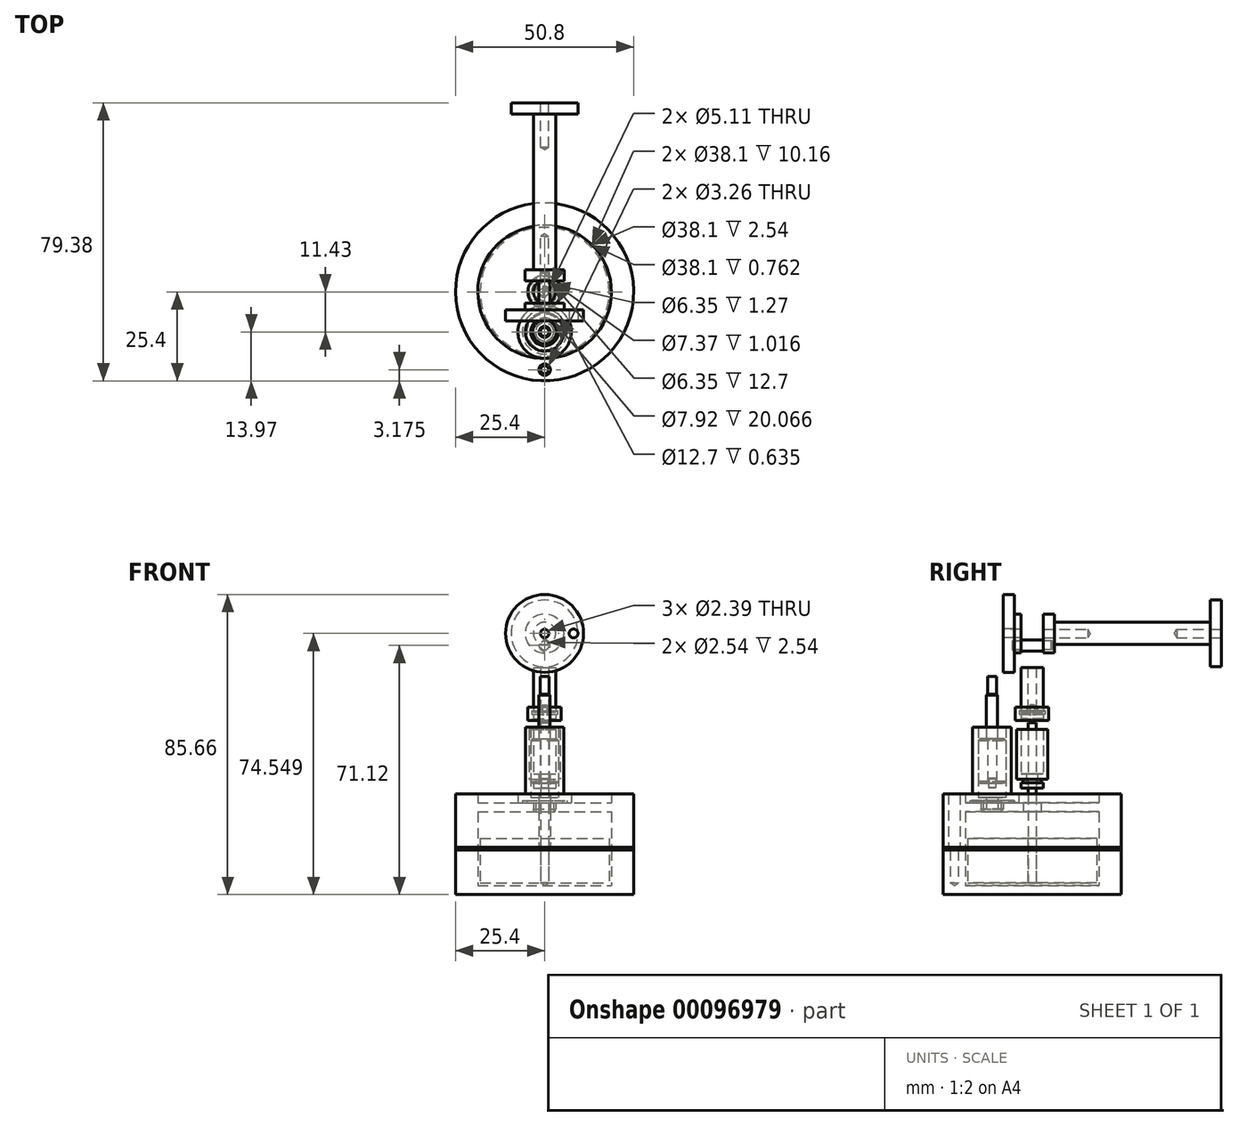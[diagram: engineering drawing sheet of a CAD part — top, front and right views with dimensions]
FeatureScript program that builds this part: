
annotation { "Feature Type Name" : "Feature", "Feature Type Description" : "" }
export const myFeature = defineFeature(function(context is Context, id is Id, definition is map)
    precondition{}
    {
        {
            assignVariable(context, id + "F0", {"name" : "RevolveDeg", "anyValue" : 360});
        }
        {
            var Q0;
            Q0=qCreatedBy(makeId("Right.planeOp"),FACE);
            var sketch = newSketch(context, id + "F1", { "sketchPlane" : qUnion([Q0])});
            skLineSegment(sketch, "E0", {"start": v(0, 0) * mm, "end": v(0, 183.81) * mm, "construction": true});
            skLineSegment(sketch, "E1", {"start": v(0, 0) * mm, "end": v(25.4, 0) * mm});
            skLineSegment(sketch, "E2", {"start": v(25.4, 12.7) * mm, "end": v(19.05, 12.7) * mm});
            skLineSegment(sketch, "E3", {"start": v(19.05, 12.7) * mm, "end": v(19.05, 2.54) * mm});
            skLineSegment(sketch, "E4", {"start": v(19.05, 2.54) * mm, "end": v(0, 2.54) * mm});
            skLineSegment(sketch, "E5", {"start": v(0, 2.54) * mm, "end": v(0, 0) * mm});
            skLineSegment(sketch, "E6", {"start": v(25.4, 12.7) * mm, "end": v(25.4, 0) * mm});
            skSolve(sketch);
        }
        {
            var Q0;
            Q0=qSketchRegion(id+"F1",true);
            var Q1;
            Q1=sQuery(id+"F1.wireOp",EDGE,"E0");
            revolve(context, id + "F2", {"entities" : qUnion([Q0]), "axis" : qUnion([Q1]), "revolveType" : RevolveType.ONE_DIRECTION, "angle" : (getVariable(context, 'RevolveDeg')) * degree});
        }
        {
            var Q0;
            Q0=qCreatedBy(makeId("Right.planeOp"),FACE);
            var sketch = newSketch(context, id + "F3", { "sketchPlane" : qUnion([Q0])});
            skLineSegment(sketch, "E7", {"start": v(0, 0) * mm, "end": v(0, 44.02) * mm, "construction": true});
            skLineSegment(sketch, "E8.bottom", {"start": v(19.05, 13.46) * mm, "end": v(25.4, 13.46) * mm});
            skLineSegment(sketch, "E8.top", {"start": v(19.05, 12.7) * mm, "end": v(25.4, 12.7) * mm});
            skLineSegment(sketch, "E8.left", {"start": v(19.05, 13.46) * mm, "end": v(19.05, 12.7) * mm});
            skLineSegment(sketch, "E8.right", {"start": v(25.4, 13.46) * mm, "end": v(25.4, 12.7) * mm});
            skSolve(sketch);
        }
        {
            var Q0;
            Q0=qSketchRegion(id+"F3",true);
            var Q1;
            Q1=sQuery(id+"F1.wireOp",EDGE,"E0");
            revolve(context, id + "F4", {"entities" : qUnion([Q0]), "axis" : qUnion([Q1]), "revolveType" : RevolveType.ONE_DIRECTION, "angle" : (getVariable(context, 'RevolveDeg')) * degree});
        }
        {
            var Q0;
            Q0=qCreatedBy(makeId("Right.planeOp"),FACE);
            var sketch = newSketch(context, id + "F5", { "sketchPlane" : qUnion([Q0])});
            skLineSegment(sketch, "E9", {"start": v(0, 0) * mm, "end": v(0, 65.3) * mm, "construction": true});
            skLineSegment(sketch, "E10", {"start": v(2.55, 23.62) * mm, "end": v(19.05, 23.62) * mm});
            skLineSegment(sketch, "E11", {"start": v(19.05, 23.62) * mm, "end": v(19.05, 13.46) * mm});
            skLineSegment(sketch, "E12", {"start": v(19.05, 13.46) * mm, "end": v(25.4, 13.46) * mm});
            skLineSegment(sketch, "E13", {"start": v(19.05, 26.16) * mm, "end": v(2.55, 26.16) * mm});
            skLineSegment(sketch, "E14", {"start": v(19.05, 28.7) * mm, "end": v(25.4, 28.7) * mm});
            skLineSegment(sketch, "E15", {"start": v(25.4, 28.7) * mm, "end": v(25.4, 13.46) * mm});
            skLineSegment(sketch, "E16", {"start": v(2.55, 26.16) * mm, "end": v(2.55, 23.62) * mm});
            skLineSegment(sketch, "E17", {"start": v(19.05, 26.16) * mm, "end": v(19.05, 28.7) * mm});
            skSolve(sketch);
        }
        {
            var Q0;
            Q0=qSketchRegion(id+"F5",true);
            var Q1;
            Q1=sQuery(id+"F5.wireOp",EDGE,"E9");
            revolve(context, id + "F6", {"entities" : qUnion([Q0]), "axis" : qUnion([Q1]), "revolveType" : RevolveType.ONE_DIRECTION, "angle" : (getVariable(context, 'RevolveDeg')) * degree});
        }
        {
            var Q0;
            Q0=qCreatedBy(makeId("Right.planeOp"),FACE);
            var sketch = newSketch(context, id + "F7", { "sketchPlane" : qUnion([Q0])});
            skLineSegment(sketch, "E18", {"start": v(-11.43, 41.18) * mm, "end": v(-11.43, 9.69) * mm, "construction": true});
            skLineSegment(sketch, "E19", {"start": v(-11.43, 38.1) * mm, "end": v(-8.88, 38.1) * mm});
            skLineSegment(sketch, "E20", {"start": v(-8.88, 38.1) * mm, "end": v(-8.88, 19.05) * mm});
            skLineSegment(sketch, "E21", {"start": v(-8.88, 19.05) * mm, "end": v(-11.43, 19.05) * mm});
            skLineSegment(sketch, "E22", {"start": v(-11.43, 19.05) * mm, "end": v(-11.43, 38.1) * mm});
            skSolve(sketch);
        }
        {
            var Q0;
            Q0=qSketchRegion(id+"F7",true);
            var Q1;
            Q1=sQuery(id+"F7.wireOp",EDGE,"E18");
            revolve(context, id + "F8", {"operationType" : NewBodyOperationType.REMOVE, "entities" : qUnion([Q0]), "axis" : qUnion([Q1]), "revolveType" : RevolveType.FULL, "oppositeDirection" : true});
        }
        {
            var Q0;
            Q0=makeQuery(id+"F6.opRevolve","SWEPT_FACE",FACE,{"disambiguationData":[OSD([sQuery(id+"F5.wireOp",EDGE,"E14")])]});
            var sketch = newSketch(context, id + "F9", { "sketchPlane" : qUnion([Q0])});
            skLineSegment(sketch, "E23", {"start": v(0, 0) * mm, "end": v(0, -22.23) * mm, "construction": true});
            skSolve(sketch);
        }
        {
            var Q0;
            Q0=sQuery(id+"F9.wireOp",VERTEX,"E23.end");
            var Q1;
            Q1=makeQuery(id+"F6.opRevolve","SWEPT_BODY",BODY,{"disambiguationData":[OSD([sQuery(id+"F5.wireOp",EDGE,"E10"),sQuery(id+"F5.wireOp",EDGE,"E11"),sQuery(id+"F5.wireOp",EDGE,"E12"),sQuery(id+"F5.wireOp",EDGE,"08VaniDS-F7S3-UYdR-9gwU-UklKb1meRO1m"),sQuery(id+"F5.wireOp",EDGE,"E13"),sQuery(id+"F5.wireOp",EDGE,"VDbhP0wL-WkEG-9tpd-pb4e-fJYebzpu9ne2"),sQuery(id+"F5.wireOp",EDGE,"1rfxJHBh-3GeA-Al4Y-TgrG-wPFw9h637zQ4"),sQuery(id+"F5.wireOp",EDGE,"KjVC7eHJ-TeH3-lBgi-2ye4-55toui7hDt7F"),sQuery(id+"F5.wireOp",EDGE,"E14"),sQuery(id+"F5.wireOp",EDGE,"E15"),sQuery(id+"F5.wireOp",EDGE,"Vt3FRohS-Tt50-dYyf-sNZV-e8CKWPU7Xsff"),sQuery(id+"F5.wireOp",EDGE,"E16"),sQuery(id+"F5.wireOp",EDGE,"d1I6BEPt-4xFZ-tPL8-wAWT-zq3UIMwmx8vm"),sQuery(id+"F5.wireOp",EDGE,"D6rHBlV9-BTCJ-jmse-U5A9-QZR0yaPT5cx9"),sQuery(id+"F5.wireOp",EDGE,"EEDruurF-CJB4-QrCg-3RPu-BX3cZhrb5usn"),sQuery(id+"F5.wireOp",EDGE,"10icGVZa-xdl5-e8uB-mR9X-ele6sR0L7zSO"),sQuery(id+"F5.wireOp",EDGE,"wtxHyDoK-8vKZ-d9tK-FhL2-Dx1DbIcqa6A4"),sQuery(id+"F5.wireOp",EDGE,"E17"),sQuery(id+"F5.wireOp",EDGE,"p2X2xDUn-i6el-BxTP-Kqf6-1vIeUNN4H1RK")])]});
            hole(context, id + "F10", {"style" : HoleStyle.SIMPLE, "endStyle" : HoleEndStyle.THROUGH, "standardTappedOrClearance" : lookupTablePath({ "standard" : "ANSI", "fit" : "Normal (ASME)", "size" : "#4", "type" : "Clearance" }), "standardBlindInLast" : lookupTablePath({ "fit" : "Free", "standard" : "ANSI", "size" : "#4", "type" : "Clearance" }), "holeDiameter" : 3.26 * mm, "locations" : qUnion([Q0]), "scope" : qUnion([Q1]), "isTappedThrough" : true});
        }
        {
            var Q0;
            Q0=sQuery(id+"F9.wireOp",VERTEX,"E23.end");
            var Q1;
            Q1=makeQuery(id+"F4.opRevolve","SWEPT_BODY",BODY,{"disambiguationData":[OSD([sQuery(id+"F3.wireOp",EDGE,"E8.bottom"),sQuery(id+"F3.wireOp",EDGE,"E8.top"),sQuery(id+"F3.wireOp",EDGE,"E8.left"),sQuery(id+"F3.wireOp",EDGE,"E8.right")])]});
            hole(context, id + "F11", {"style" : HoleStyle.SIMPLE, "endStyle" : HoleEndStyle.THROUGH, "standardTappedOrClearance" : lookupTablePath({ "standard" : "ANSI", "fit" : "Normal (ASME)", "size" : "#4", "type" : "Clearance" }), "standardBlindInLast" : lookupTablePath({ "fit" : "Free", "standard" : "ANSI", "size" : "#4", "type" : "Clearance" }), "holeDiameter" : 3.26 * mm, "locations" : qUnion([Q0]), "scope" : qUnion([Q1]), "isTappedThrough" : true});
        }
        {
            var Q0;
            Q0=sQuery(id+"F9.wireOp",VERTEX,"E23.end");
            var Q1;
            Q1=makeQuery(id+"F2.opRevolve","SWEPT_BODY",BODY,{"disambiguationData":[OSD([sQuery(id+"F1.wireOp",EDGE,"E1"),sQuery(id+"F1.wireOp",EDGE,"E2"),sQuery(id+"F1.wireOp",EDGE,"E3"),sQuery(id+"F1.wireOp",EDGE,"E4"),sQuery(id+"F1.wireOp",EDGE,"E5"),sQuery(id+"F1.wireOp",EDGE,"E6")])]});
            hole(context, id + "F12", {"style" : HoleStyle.SIMPLE, "endStyle" : HoleEndStyle.BLIND, "standardTappedOrClearance" : lookupTablePath({ "standard" : "ANSI", "engagement" : "75%", "pitch" : "40 tpi", "size" : "#4", "type" : "Tapped" }), "standardBlindInLast" : lookupTablePath({ "standard" : "ANSI", "engagement" : "75%", "pitch" : "40 tpi", "size" : "#4", "type" : "Tapped" }), "holeDiameter" : 2.26 * mm, "holeDepth" : 25.4 * mm, "startFromSketch" : true, "locations" : qUnion([Q0]), "scope" : qUnion([Q1]), "majorDiameter" : 2.84 * mm});
        }
        {
            var Q0;
            Q0=qCreatedBy(makeId("Right.planeOp"),FACE);
            var sketch = newSketch(context, id + "F13", { "sketchPlane" : qUnion([Q0])});
            skLineSegment(sketch, "E24", {"start": v(0, 0) * mm, "end": v(0, 55.1) * mm, "construction": true});
            skLineSegment(sketch, "E25", {"start": v(4.44, 47.15) * mm, "end": v(4.45, 32.9) * mm});
            skLineSegment(sketch, "E26", {"start": v(4.45, 32.9) * mm, "end": v(2.54, 32.9) * mm});
            skLineSegment(sketch, "E27", {"start": v(3.17, 31.88) * mm, "end": v(3.17, 30.36) * mm});
            skLineSegment(sketch, "E28", {"start": v(3.17, 30.36) * mm, "end": v(1.59, 30.36) * mm});
            skLineSegment(sketch, "E29", {"start": v(1.59, 30.36) * mm, "end": v(1.59, 34.45) * mm});
            skLineSegment(sketch, "E30", {"start": v(3.18, 47.15) * mm, "end": v(4.44, 47.15) * mm});
            skLineSegment(sketch, "E31", {"start": v(1.59, 34.45) * mm, "end": v(3.18, 34.45) * mm});
            skLineSegment(sketch, "E32", {"start": v(3.18, 34.45) * mm, "end": v(3.18, 47.15) * mm});
            skLineSegment(sketch, "E33", {"start": v(3.17, 31.88) * mm, "end": v(2.54, 31.88) * mm});
            skLineSegment(sketch, "E34", {"start": v(2.54, 31.88) * mm, "end": v(2.54, 32.9) * mm});
            skSolve(sketch);
        }
        {
            var Q0;
            Q0=makeQuery(id+"F13.imprint","IMPRINT",FACE,{"disambiguationData":[TD([[makeQuery(id+"F13.imprint","IMPRINT",EDGE,{"derivedFrom":sQuery(id+"F13.wireOp",EDGE,"E25")}),-1.0]])]});
            var Q1;
            Q1=sQuery(id+"F13.wireOp",EDGE,"E24");
            revolve(context, id + "F14", {"entities" : qUnion([Q0]), "axis" : qUnion([Q1]), "revolveType" : RevolveType.ONE_DIRECTION, "angle" : (getVariable(context, 'RevolveDeg')) * degree});
        }
        {
            var Q0;
            Q0=qCreatedBy(makeId("Right.planeOp"),FACE);
            var sketch = newSketch(context, id + "F15", { "sketchPlane" : qUnion([Q0])});
            skLineSegment(sketch, "E35", {"start": v(0, 0) * mm, "end": v(0, 53.04) * mm, "construction": true});
            skLineSegment(sketch, "E36.bottom", {"start": v(3.18, 52.13) * mm, "end": v(1.2, 52.13) * mm});
            skLineSegment(sketch, "E36.top", {"start": v(3.18, 64.83) * mm, "end": v(1.2, 64.83) * mm});
            skLineSegment(sketch, "E36.left", {"start": v(3.18, 52.13) * mm, "end": v(3.18, 64.83) * mm});
            skLineSegment(sketch, "E36.right", {"start": v(1.2, 52.13) * mm, "end": v(1.2, 64.83) * mm});
            skSolve(sketch);
        }
        {
            var Q0;
            Q0=qSketchRegion(id+"F15",true);
            var Q1;
            Q1=sQuery(id+"F15.wireOp",EDGE,"E35");
            revolve(context, id + "F16", {"entities" : qUnion([Q0]), "axis" : qUnion([Q1]), "revolveType" : RevolveType.ONE_DIRECTION, "angle" : (getVariable(context, 'RevolveDeg')) * degree});
        }
        {
            var Q0;
            Q0=qCreatedBy(makeId("Right.planeOp"),FACE);
            var sketch = newSketch(context, id + "F17", { "sketchPlane" : qUnion([Q0])});
            skLineSegment(sketch, "E37", {"start": v(0, 0) * mm, "end": v(0, 48.97) * mm, "construction": true});
            skLineSegment(sketch, "E38", {"start": v(3.17, 50.22) * mm, "end": v(3.68, 49.71) * mm});
            skLineSegment(sketch, "E39", {"start": v(3.68, 49.71) * mm, "end": v(4.76, 49.71) * mm});
            skLineSegment(sketch, "E40", {"start": v(4.76, 49.71) * mm, "end": v(4.76, 53.52) * mm});
            skLineSegment(sketch, "E41", {"start": v(4.76, 53.52) * mm, "end": v(1.52, 53.52) * mm});
            skLineSegment(sketch, "E42", {"start": v(1.52, 53.52) * mm, "end": v(1.52, 52.5) * mm});
            skLineSegment(sketch, "E43", {"start": v(1.52, 52.5) * mm, "end": v(3.68, 52.5) * mm});
            skLineSegment(sketch, "E44", {"start": v(3.17, 51.5) * mm, "end": v(3.17, 50.22) * mm});
            skLineSegment(sketch, "E45", {"start": v(3.17, 51.5) * mm, "end": v(3.68, 51.5) * mm});
            skLineSegment(sketch, "E46", {"start": v(3.68, 51.5) * mm, "end": v(3.68, 52.5) * mm});
            skSolve(sketch);
        }
        {
            var Q0;
            Q0=qSketchRegion(id+"F17",true);
            var Q1;
            Q1=sQuery(id+"F17.wireOp",EDGE,"E37");
            revolve(context, id + "F18", {"entities" : qUnion([Q0]), "axis" : qUnion([Q1]), "revolveType" : RevolveType.ONE_DIRECTION, "angle" : (getVariable(context, 'RevolveDeg')) * degree});
        }
        {
            var Q0;
            Q0=qCreatedBy(makeId("Right.planeOp"),FACE);
            var sketch = newSketch(context, id + "F19", { "sketchPlane" : qUnion([Q0])});
            skLineSegment(sketch, "E47", {"start": v(0, 0) * mm, "end": v(0, 54.6) * mm, "construction": true});
            skLineSegment(sketch, "E48.bottom", {"start": v(1.2, 3.3) * mm, "end": v(18.41, 3.3) * mm});
            skLineSegment(sketch, "E48.top", {"start": v(1.2, 16) * mm, "end": v(18.42, 16) * mm});
            skLineSegment(sketch, "E48.left", {"start": v(1.2, 3.3) * mm, "end": v(1.2, 16) * mm});
            skLineSegment(sketch, "E48.right", {"start": v(18.42, 3.3) * mm, "end": v(18.42, 16) * mm});
            skSolve(sketch);
        }
        {
            var Q0;
            Q0=qSketchRegion(id+"F19",true);
            var Q1;
            Q1=sQuery(id+"F19.wireOp",EDGE,"E47");
            revolve(context, id + "F20", {"entities" : qUnion([Q0]), "axis" : qUnion([Q1]), "revolveType" : RevolveType.ONE_DIRECTION, "angle" : (getVariable(context, 'RevolveDeg')) * degree});
        }
        {
            var Q0;
            Q0=qCreatedBy(makeId("Right.planeOp"),FACE);
            var sketch = newSketch(context, id + "F21", { "sketchPlane" : qUnion([Q0])});
            skLineSegment(sketch, "E49", {"start": v(0, 0) * mm, "end": v(0, 67.1) * mm, "construction": true});
            skLineSegment(sketch, "E50.bottom", {"start": v(0, 3.3) * mm, "end": v(1.17, 3.3) * mm});
            skLineSegment(sketch, "E50.top", {"start": v(0, 54.1) * mm, "end": v(0.63, 54.1) * mm});
            skLineSegment(sketch, "E50.left", {"start": v(0, 3.3) * mm, "end": v(0, 54.1) * mm});
            skLineSegment(sketch, "E50.right", {"start": v(1.17, 3.3) * mm, "end": v(1.17, 49.02) * mm});
            skLineSegment(sketch, "E51", {"start": v(1.17, 49.02) * mm, "end": v(0.63, 49.33) * mm});
            skLineSegment(sketch, "E52", {"start": v(0.63, 49.33) * mm, "end": v(0.63, 54.1) * mm});
            skSolve(sketch);
        }
        {
            var Q0;
            Q0=qSketchRegion(id+"F21",true);
            var Q1;
            Q1=sQuery(id+"F21.wireOp",EDGE,"E49");
            revolve(context, id + "F22", {"entities" : qUnion([Q0]), "axis" : qUnion([Q1]), "revolveType" : RevolveType.FULL});
        }
        {
            var Q0;
            Q0=qCreatedBy(makeId("Right.planeOp"),FACE);
            var sketch = newSketch(context, id + "F23", { "sketchPlane" : qUnion([Q0])});
            skLineSegment(sketch, "E53", {"start": v(-11.43, 59.37) * mm, "end": v(-11.43, -7.55) * mm, "construction": true});
            skLineSegment(sketch, "E54", {"start": v(-5.94, 47.75) * mm, "end": v(-5.94, 28.7) * mm});
            skLineSegment(sketch, "E55", {"start": v(-5.94, 28.7) * mm, "end": v(-3.81, 28.7) * mm});
            skLineSegment(sketch, "E56", {"start": v(-3.81, 28.7) * mm, "end": v(-3.81, 26.16) * mm});
            skLineSegment(sketch, "E57", {"start": v(-3.81, 26.16) * mm, "end": v(-5.08, 26.16) * mm});
            skLineSegment(sketch, "E58", {"start": v(-5.08, 26.16) * mm, "end": v(-5.08, 26.8) * mm});
            skLineSegment(sketch, "E59", {"start": v(-5.08, 26.8) * mm, "end": v(-6.35, 26.8) * mm});
            skLineSegment(sketch, "E60", {"start": v(-6.35, 26.8) * mm, "end": v(-6.35, 26.16) * mm});
            skLineSegment(sketch, "E61", {"start": v(-6.35, 26.16) * mm, "end": v(-8.26, 26.16) * mm});
            skLineSegment(sketch, "E62", {"start": v(-8.26, 26.16) * mm, "end": v(-8.26, 24.38) * mm});
            skLineSegment(sketch, "E63", {"start": v(-8.26, 24.38) * mm, "end": v(-8.53, 23.62) * mm});
            skLineSegment(sketch, "E64", {"start": v(-8.53, 23.62) * mm, "end": v(-9.78, 23.62) * mm});
            skLineSegment(sketch, "E65", {"start": v(-9.78, 23.62) * mm, "end": v(-9.78, 27.69) * mm});
            skLineSegment(sketch, "E66", {"start": v(-9.78, 27.69) * mm, "end": v(-7.47, 27.69) * mm});
            skLineSegment(sketch, "E67", {"start": v(-7.47, 27.69) * mm, "end": v(-7.47, 47.75) * mm});
            skLineSegment(sketch, "E68", {"start": v(-7.47, 47.75) * mm, "end": v(-5.94, 47.75) * mm});
            skSolve(sketch);
        }
        {
            var Q0;
            Q0=qSketchRegion(id+"F23",true);
            var Q1;
            Q1=sQuery(id+"F23.wireOp",EDGE,"E53");
            revolve(context, id + "F24", {"entities" : qUnion([Q0]), "axis" : qUnion([Q1]), "revolveType" : RevolveType.ONE_DIRECTION, "oppositeDirection" : true, "angle" : (getVariable(context, 'RevolveDeg')) * degree});
        }
        {
            var Q0;
            Q0=qCreatedBy(makeId("Right.planeOp"),FACE);
            var sketch = newSketch(context, id + "F25", { "sketchPlane" : qUnion([Q0])});
            skLineSegment(sketch, "E69", {"start": v(-11.43, -7.77) * mm, "end": v(-11.43, 61.16) * mm, "construction": true});
            skLineSegment(sketch, "E70.bottom", {"start": v(-10.13, 31.75) * mm, "end": v(-7.5, 31.75) * mm});
            skLineSegment(sketch, "E70.top", {"start": v(-10.13, 44.45) * mm, "end": v(-7.5, 44.45) * mm});
            skLineSegment(sketch, "E70.left", {"start": v(-10.13, 31.75) * mm, "end": v(-10.13, 44.45) * mm});
            skLineSegment(sketch, "E70.right", {"start": v(-7.5, 31.75) * mm, "end": v(-7.5, 44.45) * mm});
            skSolve(sketch);
        }
        {
            var Q0;
            Q0=qSketchRegion(id+"F25",true);
            var Q1;
            Q1=sQuery(id+"F25.wireOp",EDGE,"E69");
            revolve(context, id + "F26", {"entities" : qUnion([Q0]), "axis" : qUnion([Q1]), "revolveType" : RevolveType.ONE_DIRECTION, "angle" : (getVariable(context, 'RevolveDeg')) * degree});
        }
        {
            var Q0;
            Q0=makeQuery(id+"F26.opRevolve","SWEPT_EDGE",EDGE,{"disambiguationData":[OSD([sQuery(id+"F25.wireOp",EDGE,"E70.top"),sQuery(id+"F25.wireOp",EDGE,"E70.right")])]});
            var Q1;
            Q1=makeQuery(id+"F26.opRevolve","SWEPT_EDGE",EDGE,{"disambiguationData":[OSD([sQuery(id+"F25.wireOp",EDGE,"E70.bottom"),sQuery(id+"F25.wireOp",EDGE,"E70.right")])]});
            chamfer(context, id + "F27", {"entities" : qUnion([Q0, Q1]), "width" : 0.5 * mm});
        }
        {
            var Q0;
            Q0=qCreatedBy(makeId("Right.planeOp"),FACE);
            var sketch = newSketch(context, id + "F28", { "sketchPlane" : qUnion([Q0])});
            skLineSegment(sketch, "E71", {"start": v(-11.43, -10.62) * mm, "end": v(-11.43, 63.7) * mm, "construction": true});
            skLineSegment(sketch, "E72.bottom", {"start": v(-11.43, 30.48) * mm, "end": v(-10.41, 30.48) * mm});
            skLineSegment(sketch, "E72.left", {"start": v(-11.43, 30.48) * mm, "end": v(-11.43, 62.23) * mm});
            skLineSegment(sketch, "E72.right", {"start": v(-9.84, 44.45) * mm, "end": v(-9.84, 56.97) * mm});
            skLineSegment(sketch, "E73", {"start": v(-9.84, 56.97) * mm, "end": v(-10.16, 57.15) * mm});
            skLineSegment(sketch, "E74", {"start": v(-10.16, 57.15) * mm, "end": v(-10.16, 62.23) * mm});
            skLineSegment(sketch, "E75", {"start": v(-10.16, 62.23) * mm, "end": v(-11.43, 62.23) * mm});
            skLineSegment(sketch, "E76", {"start": v(-9.84, 44.45) * mm, "end": v(-10.16, 44.45) * mm});
            skLineSegment(sketch, "E77", {"start": v(-10.16, 44.45) * mm, "end": v(-10.16, 33.17) * mm});
            skLineSegment(sketch, "E78", {"start": v(-10.16, 33.17) * mm, "end": v(-10.41, 33.02) * mm});
            skLineSegment(sketch, "E79", {"start": v(-10.41, 33.02) * mm, "end": v(-10.41, 30.48) * mm});
            skSolve(sketch);
        }
        {
            var Q0;
            Q0=qSketchRegion(id+"F28",true);
            var Q1;
            Q1=sQuery(id+"F28.wireOp",EDGE,"E71");
            revolve(context, id + "F29", {"entities" : qUnion([Q0]), "axis" : qUnion([Q1]), "revolveType" : RevolveType.ONE_DIRECTION, "angle" : 360 * degree});
        }
        {
            var Q0;
            Q0=qCreatedBy(makeId("Right.planeOp"),FACE);
            var sketch = newSketch(context, id + "F30", { "sketchPlane" : qUnion([Q0])});
            skLineSegment(sketch, "E80", {"start": v(-88.87, 74.55) * mm, "end": v(85.8, 74.55) * mm, "construction": true});
            skLineSegment(sketch, "E81", {"start": v(-11.43, -16.55) * mm, "end": v(-11.43, 125.12) * mm, "construction": true});
            skLineSegment(sketch, "E82", {"start": v(0, 0) * mm, "end": v(0, 126.37) * mm, "construction": true});
            skLineSegment(sketch, "E83", {"start": v(-8.26, 85.66) * mm, "end": v(-8.26, 75.74) * mm});
            skLineSegment(sketch, "E84", {"start": v(-8.26, 75.74) * mm, "end": v(-3.18, 75.74) * mm});
            skLineSegment(sketch, "E85", {"start": v(-3.18, 75.74) * mm, "end": v(-3.18, 80.1) * mm});
            skLineSegment(sketch, "E86", {"start": v(-3.18, 80.1) * mm, "end": v(-6.35, 80.1) * mm});
            skLineSegment(sketch, "E87", {"start": v(-6.35, 80.1) * mm, "end": v(-6.35, 77.72) * mm});
            skLineSegment(sketch, "E88", {"start": v(-5.08, 77.72) * mm, "end": v(-6.35, 77.72) * mm});
            skLineSegment(sketch, "E89", {"start": v(-5.08, 77.72) * mm, "end": v(-5.08, 85.66) * mm});
            skLineSegment(sketch, "E90", {"start": v(-5.08, 85.66) * mm, "end": v(-8.26, 85.66) * mm});
            skSolve(sketch);
        }
        {
            var Q0;
            Q0=qSketchRegion(id+"F30",true);
            var Q1;
            Q1=sQuery(id+"F30.wireOp",EDGE,"E80");
            revolve(context, id + "F31", {"entities" : qUnion([Q0]), "axis" : qUnion([Q1]), "revolveType" : RevolveType.FULL});
        }
        {
            var Q0;
            Q0=makeQuery(id+"F31.opRevolve","SWEPT_FACE",FACE,{"disambiguationData":[OSD([sQuery(id+"F30.wireOp",EDGE,"E85")])]});
            var sketch = newSketch(context, id + "F32", { "sketchPlane" : qUnion([Q0])});
            skCircle(sketch, "E91", {"center": v(0, 71.12) * mm, "radius": 1.27 * mm});
            skLineSegment(sketch, "E92", {"start": v(0, 71.12) * mm, "end": v(0, 74.55) * mm, "construction": true});
            skLineSegment(sketch, "E93", {"start": v(0, 74.55) * mm, "end": v(20.69, 74.55) * mm, "construction": true});
            skSolve(sketch);
        }
        {
            var Q0;
            Q0=qSketchRegion(id+"F32",true);
            extrude(context, id + "F33", {"entities" : qUnion([Q0]), "operationType" : NewBodyOperationType.REMOVE, "oppositeDirection" : true, "depth" : 2.54 * mm});
        }
        {
            var Q0;
            Q0=makeQuery(id+"F31.opRevolve","SWEPT_FACE",FACE,{"disambiguationData":[OSD([sQuery(id+"F30.wireOp",EDGE,"E83")])]});
            var sketch = newSketch(context, id + "F34", { "sketchPlane" : qUnion([Q0])});
            skLineSegment(sketch, "E94", {"start": v(0, 111.9) * mm, "end": v(0, 74.55) * mm, "construction": true});
            skLineSegment(sketch, "E95", {"start": v(0, 74.55) * mm, "end": v(8.26, 74.55) * mm, "construction": true});
            skCircle(sketch, "E96", {"center": v(8.26, 74.55) * mm, "radius": 1.27 * mm});
            skSolve(sketch);
        }
        {
            var Q0;
            Q0=qSketchRegion(id+"F34",true);
            var Q1;
            Q1=sQuery(id+"F34.wireOp",EDGE,"E96");
            extrude(context, id + "F35", {"entities" : qUnion([Q0]), "operationType" : NewBodyOperationType.REMOVE, "surfaceEntities" : qUnion([Q1]), "oppositeDirection" : true, "depth" : 5.08 * mm});
        }
        {
            var Q0;
            Q0=qCreatedBy(makeId("Right.planeOp"),FACE);
            var sketch = newSketch(context, id + "F36", { "sketchPlane" : qUnion([Q0])});
            skLineSegment(sketch, "E97", {"start": v(3.18, 80.1) * mm, "end": v(3.18, 75.74) * mm});
            skLineSegment(sketch, "E98", {"start": v(3.18, 75.74) * mm, "end": v(15.88, 75.74) * mm});
            skLineSegment(sketch, "E99", {"start": v(53.98, 75.74) * mm, "end": v(53.98, 84.07) * mm});
            skLineSegment(sketch, "E100", {"start": v(53.98, 84.07) * mm, "end": v(50.8, 84.07) * mm});
            skLineSegment(sketch, "E101", {"start": v(50.8, 84.07) * mm, "end": v(50.8, 77.72) * mm});
            skLineSegment(sketch, "E102", {"start": v(50.8, 77.72) * mm, "end": v(6.35, 77.72) * mm});
            skLineSegment(sketch, "E103", {"start": v(6.35, 77.72) * mm, "end": v(6.35, 80.1) * mm});
            skLineSegment(sketch, "E104", {"start": v(6.35, 80.1) * mm, "end": v(3.18, 80.1) * mm});
            skLineSegment(sketch, "E105", {"start": v(0, 93.62) * mm, "end": v(0, 55.48) * mm, "construction": true});
            skLineSegment(sketch, "E106", {"start": v(86.06, 74.55) * mm, "end": v(-79.26, 74.55) * mm, "construction": true});
            skPoint(sketch, "E106.endSnap0", {"position": v(0, 74.55) * mm});
            skLineSegment(sketch, "E107", {"start": v(15.88, 75.74) * mm, "end": v(16.6, 74.55) * mm});
            skLineSegment(sketch, "E108", {"start": v(16.6, 74.55) * mm, "end": v(40.56, 74.55) * mm});
            skLineSegment(sketch, "E109", {"start": v(40.56, 74.55) * mm, "end": v(41.28, 75.74) * mm});
            skLineSegment(sketch, "E110.trimOffspring", {"start": v(41.28, 75.74) * mm, "end": v(53.98, 75.74) * mm});
            skSolve(sketch);
        }
        {
            var Q0;
            Q0=qSketchRegion(id+"F36",true);
            var Q1;
            Q1=sQuery(id+"F36.wireOp",EDGE,"E106");
            revolve(context, id + "F37", {"entities" : qUnion([Q0]), "axis" : qUnion([Q1]), "revolveType" : RevolveType.FULL});
        }
        {
            var Q0;
            Q0=makeQuery(id+"F37.opRevolve","SWEPT_FACE",FACE,{"disambiguationData":[OSD([sQuery(id+"F36.wireOp",EDGE,"E97")])]});
            var sketch = newSketch(context, id + "F38", { "sketchPlane" : qUnion([Q0])});
            skCircle(sketch, "E111", {"center": v(0, 71.12) * mm, "radius": 1.27 * mm});
            skLineSegment(sketch, "E112", {"start": v(0, 71.12) * mm, "end": v(0, 74.55) * mm, "construction": true});
            skLineSegment(sketch, "E113", {"start": v(0, 74.55) * mm, "end": v(19.55, 74.55) * mm, "construction": true});
            skSolve(sketch);
        }
        {
            var Q0;
            Q0=makeQuery(id+"F38.imprint","IMPRINT",FACE,{"disambiguationData":[TD([[makeQuery(id+"F38.imprint","IMPRINT",EDGE,{"derivedFrom":sQuery(id+"F38.wireOp",EDGE,"E111")}),1.0]])]});
            extrude(context, id + "F39", {"entities" : qUnion([Q0]), "operationType" : NewBodyOperationType.REMOVE, "oppositeDirection" : true, "depth" : 2.54 * mm});
        }
        {
            var Q0;
            Q0=qCreatedBy(makeId("Right.planeOp"),FACE);
            var sketch = newSketch(context, id + "F40", { "sketchPlane" : qUnion([Q0])});
            skLineSegment(sketch, "E114", {"start": v(0, 0) * mm, "end": v(0, 135) * mm, "construction": true});
            skLineSegment(sketch, "E115", {"start": v(-47.28, 74.55) * mm, "end": v(75.1, 74.55) * mm, "construction": true});
            skLineSegment(sketch, "E116", {"start": v(-7.35, 71.12) * mm, "end": v(8.28, 71.12) * mm, "construction": true});
            skLineSegment(sketch, "E117", {"start": v(-5.46, 72.4) * mm, "end": v(-3.17, 72.4) * mm});
            skLineSegment(sketch, "E118", {"start": v(-3.17, 72.4) * mm, "end": v(-3.17, 72.7) * mm});
            skLineSegment(sketch, "E119", {"start": v(-3.17, 72.7) * mm, "end": v(3.17, 72.7) * mm});
            skLineSegment(sketch, "E120", {"start": v(3.18, 72.7) * mm, "end": v(3.18, 72.4) * mm});
            skLineSegment(sketch, "E121", {"start": v(3.17, 72.4) * mm, "end": v(5.46, 72.4) * mm});
            skLineSegment(sketch, "E122", {"start": v(5.46, 72.4) * mm, "end": v(5.46, 71.12) * mm});
            skLineSegment(sketch, "E123", {"start": v(5.46, 71.12) * mm, "end": v(-5.46, 71.12) * mm});
            skLineSegment(sketch, "E124", {"start": v(-5.46, 71.12) * mm, "end": v(-5.46, 72.4) * mm});
            skPoint(sketch, "E125", {"position": v(0, 72.7) * mm});
            skSolve(sketch);
        }
        {
            var Q0;
            Q0=makeQuery(id+"F40.imprint","IMPRINT",FACE,{"disambiguationData":[TD([[makeQuery(id+"F40.imprint","IMPRINT",EDGE,{"derivedFrom":sQuery(id+"F40.wireOp",EDGE,"E117")}),-1.0]])]});
            var Q1;
            Q1=sQuery(id+"F40.wireOp",EDGE,"E116");
            revolve(context, id + "F41", {"entities" : qUnion([Q0]), "axis" : qUnion([Q1]), "revolveType" : RevolveType.FULL});
        }
    });
